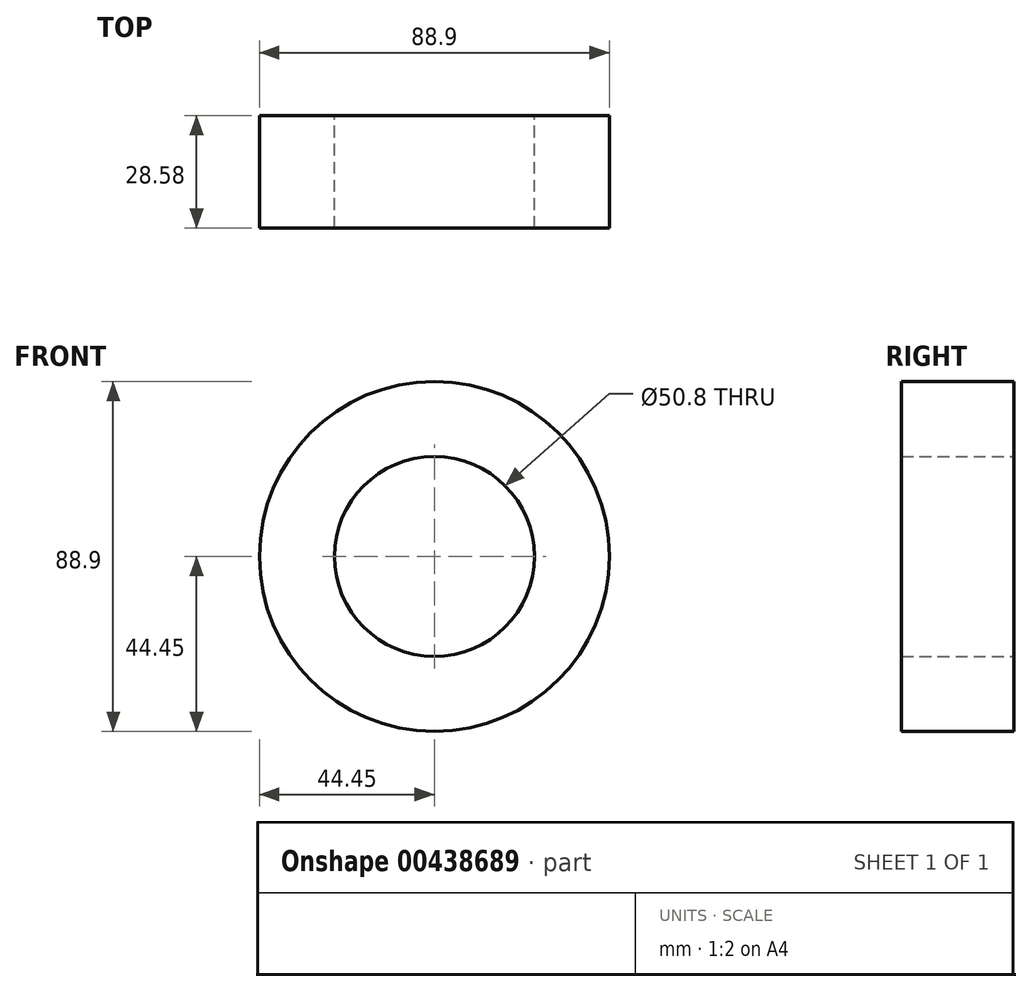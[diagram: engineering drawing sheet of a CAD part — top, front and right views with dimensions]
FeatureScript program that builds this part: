
annotation { "Feature Type Name" : "Feature", "Feature Type Description" : "" }
export const myFeature = defineFeature(function(context is Context, id is Id, definition is map)
    precondition{}
    {
        {
            var Q0;
            Q0=qCreatedBy(makeId("Front.planeOp"),FACE);
            var sketch = newSketch(context, id + "F0", { "sketchPlane" : qUnion([Q0])});
            skCircle(sketch, "E0", {"center": v(0, 0) * mm, "radius": 25.4 * mm});
            skCircle(sketch, "E1", {"center": v(0, 0) * mm, "radius": 44.45 * mm});
            skSolve(sketch);
        }
        {
            var Q0;
            Q0=sQuery(id+"F0.wireOp",EDGE,"E0");
            extrude(context, id + "F1", {"bodyType" : ToolBodyType.SURFACE, "surfaceEntities" : qUnion([Q0]), "depth" : 38.1 * mm});
        }
        {
            var Q0;
            Q0=makeQuery(id+"F0.imprint","IMPRINT",FACE,{"disambiguationData":[TD([[makeQuery(id+"F0.imprint","IMPRINT",EDGE,{"derivedFrom":sQuery(id+"F0.wireOp",EDGE,"E0")}),-1.0]])]});
            extrude(context, id + "F2", {"entities" : qUnion([Q0]), "depth" : 3.17 * mm});
        }
        {
            var Q0;
            Q0=qSketchRegion(id+"F0",true);
            var Q1;
            Q1=makeQuery(id+"F2.opExtrude","CAP_FACE",FACE,{"disambiguationData":[OSD([sQuery(id+"F0.wireOp",EDGE,"E0"),sQuery(id+"F0.wireOp",EDGE,"E1")])],"isStart":false});
            extrude(context, id + "F3", {"entities" : qUnion([Q0, Q1]), "operationType" : NewBodyOperationType.ADD, "depth" : 25.4 * mm});
        }
    });
